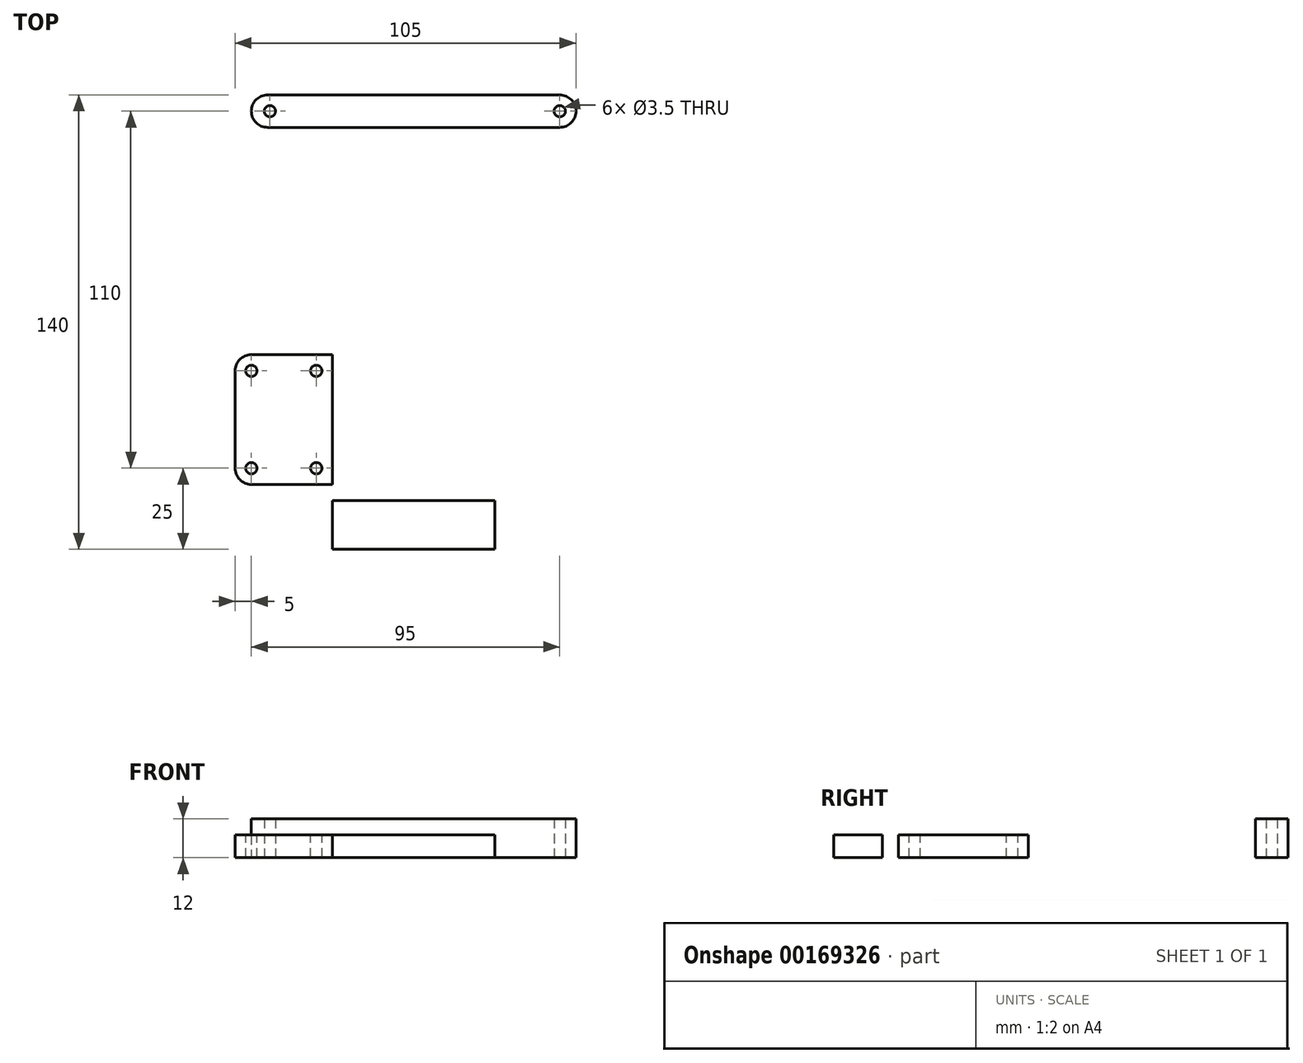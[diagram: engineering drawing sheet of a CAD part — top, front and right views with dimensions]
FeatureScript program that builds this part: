
annotation { "Feature Type Name" : "Feature", "Feature Type Description" : "" }
export const myFeature = defineFeature(function(context is Context, id is Id, definition is map)
    precondition{}
    {
        {
            var Q0;
            Q0=qCreatedBy(makeId("Top.planeOp"),FACE);
            var sketch = newSketch(context, id + "F0", { "sketchPlane" : qUnion([Q0])});
            skLineSegment(sketch, "E0.bottom", {"start": v(25, 65) * mm, "end": v(-25, 65) * mm});
            skLineSegment(sketch, "E0.top", {"start": v(25, -65) * mm, "end": v(-25, -65) * mm});
            skLineSegment(sketch, "E0.left", {"start": v(25, 65) * mm, "end": v(25, -65) * mm});
            skLineSegment(sketch, "E0.right", {"start": v(-25, 65) * mm, "end": v(-25, -65) * mm});
            skPoint(sketch, "E0.middle", {"position": v(0, 0) * mm});
            skLineSegment(sketch, "E1.bottom", {"start": v(15.25, 27.5) * mm, "end": v(-15.25, 27.5) * mm});
            skLineSegment(sketch, "E1.top", {"start": v(15.25, 40) * mm, "end": v(-15.25, 40) * mm});
            skLineSegment(sketch, "E1.left", {"start": v(15.25, 27.5) * mm, "end": v(15.25, 40) * mm});
            skLineSegment(sketch, "E1.right", {"start": v(-15.25, 27.5) * mm, "end": v(-15.25, 40) * mm});
            skPoint(sketch, "E1.middle", {"position": v(0, 33.75) * mm});
            skLineSegment(sketch, "E2.bottom", {"start": v(45, 65) * mm, "end": v(-45, 65) * mm});
            skLineSegment(sketch, "E2.top", {"start": v(45, 75) * mm, "end": v(-45, 75) * mm});
            skLineSegment(sketch, "E2.left", {"start": v(50, 70) * mm, "end": v(50, 70) * mm});
            skLineSegment(sketch, "E2.right", {"start": v(-50, 70) * mm, "end": v(-50, 70) * mm});
            skPoint(sketch, "E2.middle", {"position": v(0, 70) * mm});
            skCircle(sketch, "E3", {"center": v(-44.29, 70) * mm, "radius": 1.75 * mm});
            skPoint(sketch, "E3.centerSnap0", {"position": v(-50, 70) * mm});
            skPoint(sketch, "E4.visualSharp", {"position": v(-50, 75) * mm});
            skArc(sketch, "E4.filletArc", {"start": v(-45, 75) * mm, "mid": v(-48.54, 73.54) * mm, "end": v(-50, 70) * mm});
            skPoint(sketch, "E5.visualSharp", {"position": v(-50, 65) * mm});
            skArc(sketch, "E5.filletArc", {"start": v(-50, 70) * mm, "mid": v(-48.54, 66.46) * mm, "end": v(-45, 65) * mm});
            skPoint(sketch, "E6.visualSharp", {"position": v(50, 65) * mm});
            skArc(sketch, "E6.filletArc", {"start": v(45, 65) * mm, "mid": v(48.54, 66.46) * mm, "end": v(50, 70) * mm});
            skPoint(sketch, "E7.visualSharp", {"position": v(50, 75) * mm});
            skArc(sketch, "E7.filletArc", {"start": v(50, 70) * mm, "mid": v(48.54, 73.54) * mm, "end": v(45, 75) * mm});
            skCircle(sketch, "E8", {"center": v(45, 70) * mm, "radius": 1.75 * mm});
            skCircle(sketch, "E9", {"center": v(-18.25, 33.75) * mm, "radius": 1.25 * mm});
            skCircle(sketch, "E10", {"center": v(18.25, 33.75) * mm, "radius": 1.25 * mm});
            skLineSegment(sketch, "E11.bottom", {"start": v(-25, -5) * mm, "end": v(-55, -5) * mm});
            skLineSegment(sketch, "E11.top", {"start": v(-25, -45) * mm, "end": v(-55, -45) * mm});
            skLineSegment(sketch, "E11.left", {"start": v(-25, -5) * mm, "end": v(-25, -45) * mm});
            skLineSegment(sketch, "E11.right", {"start": v(-55, -5) * mm, "end": v(-55, -45) * mm});
            skLineSegment(sketch, "E12.bottom", {"start": v(-22, 16) * mm, "end": v(-18.9, 16) * mm});
            skLineSegment(sketch, "E12.top", {"start": v(-22, 8) * mm, "end": v(-18.9, 8) * mm});
            skLineSegment(sketch, "E12.left", {"start": v(-22, 16) * mm, "end": v(-22, 8) * mm});
            skLineSegment(sketch, "E12.right", {"start": v(-18.9, 16) * mm, "end": v(-18.9, 8) * mm});
            skLineSegment(sketch, "E13.bottom", {"start": v(-22, -37) * mm, "end": v(-18.9, -37) * mm});
            skLineSegment(sketch, "E13.top", {"start": v(-22, -45) * mm, "end": v(-18.9, -45) * mm});
            skLineSegment(sketch, "E13.left", {"start": v(-22, -37) * mm, "end": v(-22, -45) * mm});
            skLineSegment(sketch, "E13.right", {"start": v(-18.9, -37) * mm, "end": v(-18.9, -45) * mm});
            skLineSegment(sketch, "E14.bottom", {"start": v(18.9, 16) * mm, "end": v(22, 16) * mm});
            skLineSegment(sketch, "E14.top", {"start": v(18.9, 8) * mm, "end": v(22, 8) * mm});
            skLineSegment(sketch, "E14.left", {"start": v(18.9, 16) * mm, "end": v(18.9, 8) * mm});
            skLineSegment(sketch, "E14.right", {"start": v(22, 16) * mm, "end": v(22, 8) * mm});
            skLineSegment(sketch, "E15.bottom", {"start": v(18.9, -37) * mm, "end": v(22, -37) * mm});
            skLineSegment(sketch, "E15.top", {"start": v(18.9, -45) * mm, "end": v(22, -45) * mm});
            skLineSegment(sketch, "E15.left", {"start": v(18.9, -37) * mm, "end": v(18.9, -45) * mm});
            skLineSegment(sketch, "E15.right", {"start": v(22, -37) * mm, "end": v(22, -45) * mm});
            skLineSegment(sketch, "E16.top", {"start": v(25, -50) * mm, "end": v(-25, -50) * mm});
            skLineSegment(sketch, "E16.left", {"start": v(25, -65) * mm, "end": v(25, -50) * mm});
            skLineSegment(sketch, "E16.right", {"start": v(-25, -65) * mm, "end": v(-25, -50) * mm});
            skLineSegment(sketch, "E17.bottom", {"start": v(-15.25, 35.75) * mm, "end": v(-16.25, 35.75) * mm});
            skLineSegment(sketch, "E17.top", {"start": v(-15.25, 31.75) * mm, "end": v(-16.25, 31.75) * mm});
            skLineSegment(sketch, "E17.left", {"start": v(-15.25, 35.75) * mm, "end": v(-15.25, 31.75) * mm});
            skLineSegment(sketch, "E17.right", {"start": v(-16.25, 35.75) * mm, "end": v(-16.25, 31.75) * mm});
            skSolve(sketch);
        }
        {
            var Q0;
            Q0=makeQuery(id+"F0.imprint","IMPRINT",FACE,{"disambiguationData":[TD([[makeQuery(id+"F0.imprint","IMPRINT",EDGE,{"derivedFrom":sQuery(id+"F0.wireOp",EDGE,"E0.top")}),-1.0]])]});
            var Q1;
            {var subQ5=sQuery(id+"F0.wireOp",EDGE,"E0.left");Q1=makeQuery(id+"F0.imprint","IMPRINT",FACE,{"disambiguationData":[TD([[makeQuery(id+"F0.imprint","IMPRINT",EDGE,{"derivedFrom":subQ5}),-1.0]])]});}
            extrude(context, id + "F1", {"entities" : qUnion([Q0, Q1]), "depth" : 7 * mm});
        }
        {
            var Q0;
            Q0=makeQuery(id+"F0.imprint","IMPRINT",FACE,{"disambiguationData":[TD([[makeQuery(id+"F0.imprint","IMPRINT",EDGE,{"derivedFrom":sQuery(id+"F0.wireOp",EDGE,"E2.top")}),1.0]])]});
            extrude(context, id + "F2", {"entities" : qUnion([Q0]), "operationType" : NewBodyOperationType.ADD, "depth" : 12 * mm});
        }
        {
            var Q0;
            Q0=makeQuery(id+"F0.imprint","IMPRINT",FACE,{"disambiguationData":[TD([[makeQuery(id+"F0.imprint","IMPRINT",EDGE,{"derivedFrom":sQuery(id+"F0.wireOp",EDGE,"E11.bottom")}),1.0]])]});
            extrude(context, id + "F3", {"entities" : qUnion([Q0]), "operationType" : NewBodyOperationType.ADD, "depth" : 7 * mm});
        }
        {
            var Q0;
            Q0=makeQuery(id+"F3.opExtrude","SWEPT_EDGE",EDGE,{"disambiguationData":[OSD([sQuery(id+"F0.wireOp",EDGE,"E11.bottom"),sQuery(id+"F0.wireOp",EDGE,"E11.right")])]});
            var Q1;
            Q1=makeQuery(id+"F3.opExtrude","SWEPT_EDGE",EDGE,{"disambiguationData":[OSD([sQuery(id+"F0.wireOp",EDGE,"E11.top"),sQuery(id+"F0.wireOp",EDGE,"E11.right")])]});
            fillet(context, id + "F4", {"entities" : qUnion([Q0, Q1]), "radius" : 5 * mm, "tangentPropagation" : true, "allowEdgeOverflow" : false});
        }
        {
            var Q0;
            {var subQ0=sQuery(id+"F0.wireOp",EDGE,"E11.left");Q0=makeQuery(id+"F3.boolean.opBoolean","MERGE",FACE,{"derivedFrom":[makeQuery(id+"F1.opExtrude","CAP_FACE",FACE,{"disambiguationData":[OSD([sQuery(id+"F0.wireOp",EDGE,"E0.top"),sQuery(id+"F0.wireOp",EDGE,"E0.left"),sQuery(id+"F0.wireOp",EDGE,"E0.right"),sQuery(id+"F0.wireOp",EDGE,"E1.bottom"),sQuery(id+"F0.wireOp",EDGE,"E1.top"),sQuery(id+"F0.wireOp",EDGE,"E1.left"),sQuery(id+"F0.wireOp",EDGE,"E1.right"),sQuery(id+"F0.wireOp",EDGE,"E2.bottom"),sQuery(id+"F0.wireOp",EDGE,"E9"),sQuery(id+"F0.wireOp",EDGE,"E10"),subQ0,sQuery(id+"F0.wireOp",EDGE,"E12.bottom"),sQuery(id+"F0.wireOp",EDGE,"E12.top"),sQuery(id+"F0.wireOp",EDGE,"E12.left"),sQuery(id+"F0.wireOp",EDGE,"E12.right"),sQuery(id+"F0.wireOp",EDGE,"E13.bottom"),sQuery(id+"F0.wireOp",EDGE,"E13.top"),sQuery(id+"F0.wireOp",EDGE,"E13.left"),sQuery(id+"F0.wireOp",EDGE,"E13.right"),sQuery(id+"F0.wireOp",EDGE,"E14.bottom"),sQuery(id+"F0.wireOp",EDGE,"E14.top"),sQuery(id+"F0.wireOp",EDGE,"E14.left"),sQuery(id+"F0.wireOp",EDGE,"E14.right"),sQuery(id+"F0.wireOp",EDGE,"E15.bottom"),sQuery(id+"F0.wireOp",EDGE,"E15.top"),sQuery(id+"F0.wireOp",EDGE,"E15.left"),sQuery(id+"F0.wireOp",EDGE,"E15.right")])],"isStart":false}),makeQuery(id+"F3.opExtrude","CAP_FACE",FACE,{"disambiguationData":[OSD([sQuery(id+"F0.wireOp",EDGE,"E11.bottom"),sQuery(id+"F0.wireOp",EDGE,"E11.top"),subQ0,sQuery(id+"F0.wireOp",EDGE,"E11.right")])],"isStart":false})]});}
            var sketch = newSketch(context, id + "F5", { "sketchPlane" : qUnion([Q0])});
            skCircle(sketch, "E18", {"center": v(-50, -10) * mm, "radius": 1.75 * mm});
            skCircle(sketch, "E19", {"center": v(-50, -40) * mm, "radius": 1.75 * mm});
            skCircle(sketch, "E20", {"center": v(-30, -40) * mm, "radius": 1.75 * mm});
            skCircle(sketch, "E21", {"center": v(-30, -10) * mm, "radius": 1.75 * mm});
            skSolve(sketch);
        }
        {
            var Q0;
            Q0=makeQuery(id+"F5.imprint","IMPRINT",FACE,{"disambiguationData":[TD([[makeQuery(id+"F5.imprint","IMPRINT",EDGE,{"derivedFrom":sQuery(id+"F5.wireOp",EDGE,"E18")}),1.0]])]});
            var Q1;
            Q1=makeQuery(id+"F5.imprint","IMPRINT",FACE,{"disambiguationData":[TD([[makeQuery(id+"F5.imprint","IMPRINT",EDGE,{"derivedFrom":sQuery(id+"F5.wireOp",EDGE,"E21")}),1.0]])]});
            var Q2;
            Q2=makeQuery(id+"F5.imprint","IMPRINT",FACE,{"disambiguationData":[TD([[makeQuery(id+"F5.imprint","IMPRINT",EDGE,{"derivedFrom":sQuery(id+"F5.wireOp",EDGE,"E20")}),1.0]])]});
            var Q3;
            Q3=makeQuery(id+"F5.imprint","IMPRINT",FACE,{"disambiguationData":[TD([[makeQuery(id+"F5.imprint","IMPRINT",EDGE,{"derivedFrom":sQuery(id+"F5.wireOp",EDGE,"E19")}),1.0]])]});
            extrude(context, id + "F6", {"entities" : qUnion([Q0, Q1, Q2, Q3]), "operationType" : NewBodyOperationType.REMOVE, "oppositeDirection" : true, "depth" : 25 * mm});
        }
        {
            var Q0;
            Q0=makeQuery(id+"F0.imprint","IMPRINT",FACE,{"disambiguationData":[TD([[makeQuery(id+"F0.imprint","IMPRINT",EDGE,{"derivedFrom":sQuery(id+"F0.wireOp",EDGE,"E0.top")}),-1.0]])]});
            extrude(context, id + "F7", {"entities" : qUnion([Q0]), "operationType" : NewBodyOperationType.ADD, "depth" : 4 * mm});
        }
    });
